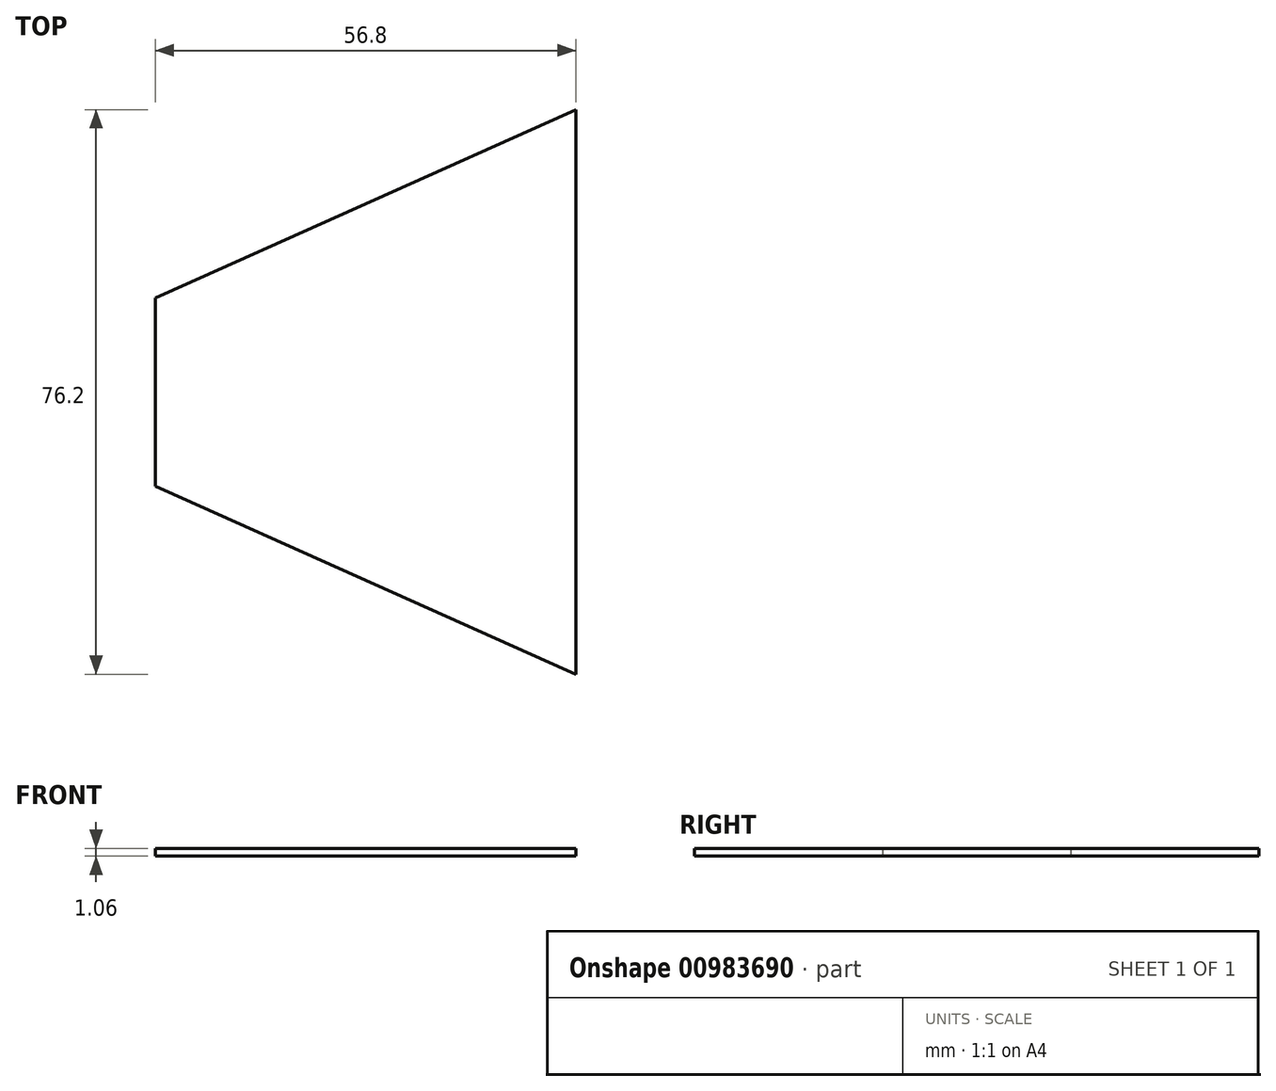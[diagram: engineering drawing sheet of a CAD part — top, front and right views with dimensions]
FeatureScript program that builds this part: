
annotation { "Feature Type Name" : "Feature", "Feature Type Description" : "" }
export const myFeature = defineFeature(function(context is Context, id is Id, definition is map)
    precondition{}
    {
        {
            var Q0;
            Q0=qCreatedBy(makeId("Top.planeOp"),FACE);
            var sketch = newSketch(context, id + "F0", { "sketchPlane" : qUnion([Q0])});
            skLineSegment(sketch, "E0.left", {"start": v(28.4, 12.7) * mm, "end": v(28.4, -12.7) * mm});
            skLineSegment(sketch, "E0.right", {"start": v(-28.4, 12.7) * mm, "end": v(-28.4, -12.7) * mm});
            skPoint(sketch, "E0.middle", {"position": v(0, 0) * mm});
            skLineSegment(sketch, "E1", {"start": v(28.4, 12.7) * mm, "end": v(28.4, 38.1) * mm});
            skLineSegment(sketch, "E2", {"start": v(28.4, 38.1) * mm, "end": v(-28.4, 12.7) * mm});
            skLineSegment(sketch, "E3", {"start": v(28.4, -12.7) * mm, "end": v(28.4, -38.1) * mm});
            skLineSegment(sketch, "E4", {"start": v(28.4, -38.1) * mm, "end": v(-28.4, -12.7) * mm});
            skSolve(sketch);
        }
        {
            var Q0;
            Q0 = qSketchRegion(id + "F0", true);
            extrude(context, id + "F1", {"entities" : qUnion([Q0]), "depth" : 1.06 * mm, "offsetDistance" : 25.4 * mm});
        }
    });
